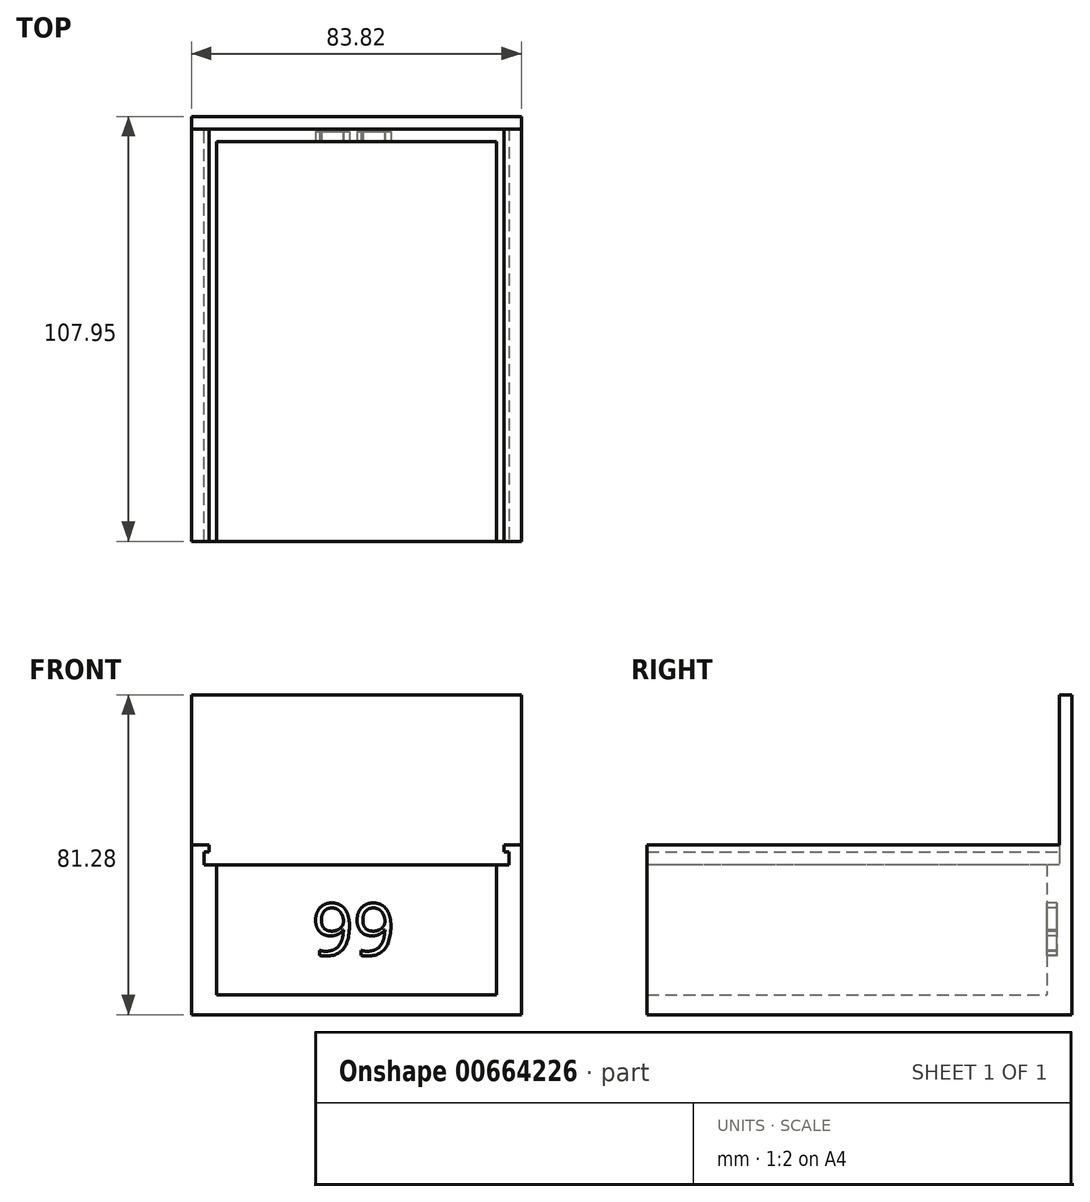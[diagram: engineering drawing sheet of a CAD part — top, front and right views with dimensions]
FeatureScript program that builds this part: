
annotation { "Feature Type Name" : "Feature", "Feature Type Description" : "" }
export const myFeature = defineFeature(function(context is Context, id is Id, definition is map)
    precondition{}
    {
        {
            var Q0;
            Q0=qCreatedBy(makeId("Top.planeOp"),FACE);
            var sketch = newSketch(context, id + "F0", { "sketchPlane" : qUnion([Q0])});
            skLineSegment(sketch, "E0.bottom", {"start": v(-35.56, 53.94) * mm, "end": v(35.56, 53.94) * mm});
            skLineSegment(sketch, "E0.top", {"start": v(-35.56, -42.58) * mm, "end": v(35.56, -42.58) * mm});
            skLineSegment(sketch, "E0.left", {"start": v(-35.56, 53.94) * mm, "end": v(-35.56, -42.58) * mm});
            skLineSegment(sketch, "E0.right", {"start": v(35.56, 53.94) * mm, "end": v(35.56, -42.58) * mm});
            skPoint(sketch, "E0.middle", {"position": v(0, 5.68) * mm});
            skLineSegment(sketch, "E1.bottom", {"start": v(-38.73, 57.11) * mm, "end": v(38.74, 57.11) * mm});
            skLineSegment(sketch, "E1.top", {"start": v(-38.74, -45.76) * mm, "end": v(38.74, -45.76) * mm});
            skLineSegment(sketch, "E1.left", {"start": v(-38.73, 57.11) * mm, "end": v(-38.74, -45.76) * mm});
            skLineSegment(sketch, "E1.right", {"start": v(38.74, 57.11) * mm, "end": v(38.74, -45.76) * mm});
            skLineSegment(sketch, "E2.bottom", {"start": v(-41.9, 60.29) * mm, "end": v(41.91, 60.29) * mm});
            skLineSegment(sketch, "E2.top", {"start": v(-41.91, -48.93) * mm, "end": v(41.91, -48.93) * mm});
            skLineSegment(sketch, "E2.left", {"start": v(-41.9, 60.29) * mm, "end": v(-41.91, -48.93) * mm});
            skLineSegment(sketch, "E2.right", {"start": v(41.91, 60.29) * mm, "end": v(41.91, -48.93) * mm});
            skLineSegment(sketch, "E3", {"start": v(-35.56, -42.58) * mm, "end": v(-41.91, -42.58) * mm});
            skLineSegment(sketch, "E4", {"start": v(35.56, -42.58) * mm, "end": v(41.91, -42.58) * mm});
            skSolve(sketch);
        }
        {
            var Q0;
            {var subQ2=sQuery(id+"F0.wireOp",EDGE,"E1.bottom");Q0=makeQuery(id+"F0.imprint","IMPRINT",FACE,{"disambiguationData":[TD([[makeQuery(id+"F0.imprint","IMPRINT",EDGE,{"derivedFrom":subQ2}),1.0]])]});}
            extrude(context, id + "F1", {"entities" : qUnion([Q0]), "depth" : 50.8 * mm, "offsetDistance" : 25.4 * mm});
        }
        {
            var Q0;
            Q0=makeQuery(id+"F0.imprint","IMPRINT",FACE,{"disambiguationData":[TD([[makeQuery(id+"F0.imprint","IMPRINT",EDGE,{"derivedFrom":sQuery(id+"F0.wireOp",EDGE,"E0.bottom")}),-1.0]])]});
            var Q1;
            Q1=makeQuery(id+"F0.imprint","IMPRINT",FACE,{"disambiguationData":[TD([[makeQuery(id+"F0.imprint","IMPRINT",EDGE,{"derivedFrom":sQuery(id+"F0.wireOp",EDGE,"E0.bottom")}),1.0]])]});
            extrude(context, id + "F2", {"entities" : qUnion([Q0, Q1]), "operationType" : NewBodyOperationType.ADD, "depth" : 12.7 * mm, "offsetDistance" : 25.4 * mm});
        }
        {
            var Q0;
            Q0=makeQuery(id+"F0.imprint","IMPRINT",FACE,{"disambiguationData":[TD([[makeQuery(id+"F0.imprint","IMPRINT",EDGE,{"derivedFrom":sQuery(id+"F0.wireOp",EDGE,"E0.bottom")}),1.0]])]});
            extrude(context, id + "F3", {"entities" : qUnion([Q0]), "operationType" : NewBodyOperationType.ADD, "depth" : 45.72 * mm, "offsetDistance" : 25.4 * mm});
        }
        {
            var Q0;
            Q0=makeQuery(id+"F1.opExtrude","SWEPT_FACE",FACE,{"disambiguationData":[OSD([sQuery(id+"F0.wireOp",EDGE,"E1.left")])]});
            var sketch = newSketch(context, id + "F4", { "sketchPlane" : qUnion([Q0])});
            skLineSegment(sketch, "E5.bottom", {"start": v(-42.58, 50.8) * mm, "end": v(57.11, 50.8) * mm});
            skLineSegment(sketch, "E5.top", {"start": v(-42.58, 49.02) * mm, "end": v(57.11, 49.02) * mm});
            skLineSegment(sketch, "E5.left", {"start": v(-42.58, 50.8) * mm, "end": v(-42.58, 49.02) * mm});
            skLineSegment(sketch, "E5.right", {"start": v(57.11, 50.8) * mm, "end": v(57.11, 49.02) * mm});
            skSolve(sketch);
        }
        {
            var Q0;
            Q0 = qSketchRegion(id + "F4", true);
            extrude(context, id + "F5", {"entities" : qUnion([Q0]), "operationType" : NewBodyOperationType.ADD, "depth" : 1.27 * mm, "offsetDistance" : 25.4 * mm});
        }
        {
            var Q0;
            Q0=makeQuery(id+"F1.opExtrude","SWEPT_FACE",FACE,{"disambiguationData":[OSD([sQuery(id+"F0.wireOp",EDGE,"E1.right")])]});
            var sketch = newSketch(context, id + "F6", { "sketchPlane" : qUnion([Q0])});
            skLineSegment(sketch, "E6.bottom", {"start": v(42.58, 50.8) * mm, "end": v(-57.11, 50.8) * mm});
            skLineSegment(sketch, "E6.top", {"start": v(42.58, 49.02) * mm, "end": v(-57.11, 49.02) * mm});
            skLineSegment(sketch, "E6.left", {"start": v(42.58, 50.8) * mm, "end": v(42.58, 49.02) * mm});
            skLineSegment(sketch, "E6.right", {"start": v(-57.11, 50.8) * mm, "end": v(-57.11, 49.02) * mm});
            skSolve(sketch);
        }
        {
            var Q0;
            Q0 = qSketchRegion(id + "F6", true);
            extrude(context, id + "F7", {"entities" : qUnion([Q0]), "operationType" : NewBodyOperationType.ADD, "depth" : 1.27 * mm, "offsetDistance" : 25.4 * mm});
        }
        {
            var Q0;
            Q0=makeQuery(id+"F3.opExtrude","SWEPT_FACE",FACE,{"disambiguationData":[OSD([sQuery(id+"F0.wireOp",EDGE,"E0.bottom")])]});
            var sketch = newSketch(context, id + "F8", { "sketchPlane" : qUnion([Q0])});
            skText(sketch, "E7", { "text": "99", "fontName": "OpenSans-Regular.ttf"});
            const initialGuessF8  = {"E7": [-0.01128, 0.02268, 1, 0, 0.01326]};
            skSetInitialGuess(sketch, initialGuessF8);
            skSolve(sketch);
        }
        {
            var Q0;
            Q0 = qSketchRegion(id + "F8", true);
            extrude(context, id + "F9", {"entities" : qUnion([Q0]), "operationType" : NewBodyOperationType.REMOVE, "oppositeDirection" : true, "depth" : 2.54 * mm, "offsetDistance" : 25.4 * mm});
        }
        {
            var Q0;
            {var subQ0=sQuery(id+"F0.wireOp",EDGE,"E4");var subQ1=sQuery(id+"F0.wireOp",EDGE,"E3");var subQ2=sQuery(id+"F0.wireOp",EDGE,"E1.right");var subQ3=sQuery(id+"F0.wireOp",EDGE,"E1.left");var subQ4=sQuery(id+"F0.wireOp",EDGE,"E1.bottom");Q0=makeQuery(id+"F2.boolean.opBoolean","MERGE",FACE,{"derivedFrom":[makeQuery(id+"F1.opExtrude","CAP_FACE",FACE,{"disambiguationData":[OSD([subQ4,subQ3,subQ2,sQuery(id+"F0.wireOp",EDGE,"E2.bottom"),sQuery(id+"F0.wireOp",EDGE,"E2.left"),sQuery(id+"F0.wireOp",EDGE,"E2.right"),subQ1,subQ0])],"isStart":true}),makeQuery(id+"F2.opExtrude","CAP_FACE",FACE,{"disambiguationData":[OSD([sQuery(id+"F0.wireOp",EDGE,"E0.top"),subQ4,subQ3,subQ2,subQ1,subQ0])],"isStart":true})]});}
            var sketch = newSketch(context, id + "F10", { "sketchPlane" : qUnion([Q0])});
            skLineSegment(sketch, "E8.bottom", {"start": v(-41.91, 42.58) * mm, "end": v(41.91, 42.58) * mm});
            skLineSegment(sketch, "E8.top", {"start": v(-41.91, -60.29) * mm, "end": v(41.91, -60.29) * mm});
            skLineSegment(sketch, "E8.left", {"start": v(-41.91, 42.58) * mm, "end": v(-41.91, -60.29) * mm});
            skLineSegment(sketch, "E8.right", {"start": v(41.91, 42.58) * mm, "end": v(41.91, -60.29) * mm});
            skSolve(sketch);
        }
        {
            var Q0;
            Q0 = qSketchRegion(id + "F10", true);
            extrude(context, id + "F11", {"entities" : qUnion([Q0]), "operationType" : NewBodyOperationType.REMOVE, "oppositeDirection" : true, "depth" : 7.62 * mm, "offsetDistance" : 25.4 * mm});
        }
        {
            var Q0;
            Q0=makeQuery(id+"F7.boolean.opBoolean","MERGE",FACE,{"derivedFrom":[makeQuery(id+"F5.boolean.opBoolean","MERGE",FACE,{"derivedFrom":[makeQuery(id+"F1.opExtrude","CAP_FACE",FACE,{"disambiguationData":[OSD([sQuery(id+"F0.wireOp",EDGE,"E1.bottom"),sQuery(id+"F0.wireOp",EDGE,"E1.left"),sQuery(id+"F0.wireOp",EDGE,"E1.right"),sQuery(id+"F0.wireOp",EDGE,"E2.bottom"),sQuery(id+"F0.wireOp",EDGE,"E2.left"),sQuery(id+"F0.wireOp",EDGE,"E2.right"),sQuery(id+"F0.wireOp",EDGE,"E3"),sQuery(id+"F0.wireOp",EDGE,"E4")])],"isStart":false}),makeQuery(id+"F5.opExtrude","SWEPT_FACE",FACE,{"disambiguationData":[OSD([sQuery(id+"F4.wireOp",EDGE,"E5.bottom")])]})]}),makeQuery(id+"F7.opExtrude","SWEPT_FACE",FACE,{"disambiguationData":[OSD([sQuery(id+"F6.wireOp",EDGE,"E6.bottom")])]})]});
            var sketch = newSketch(context, id + "F12", { "sketchPlane" : qUnion([Q0])});
            skLineSegment(sketch, "E9.bottom", {"start": v(-41.9, 60.29) * mm, "end": v(41.91, 60.29) * mm});
            skLineSegment(sketch, "E9.top", {"start": v(-41.9, 57.11) * mm, "end": v(41.91, 57.11) * mm});
            skLineSegment(sketch, "E9.left", {"start": v(-41.9, 60.29) * mm, "end": v(-41.9, 57.11) * mm});
            skLineSegment(sketch, "E9.right", {"start": v(41.91, 60.29) * mm, "end": v(41.91, 57.11) * mm});
            skSolve(sketch);
        }
        {
            var Q0;
            Q0 = qSketchRegion(id + "F12", true);
            extrude(context, id + "F13", {"entities" : qUnion([Q0]), "operationType" : NewBodyOperationType.ADD, "depth" : 38.1 * mm, "offsetDistance" : 25.4 * mm});
        }
        {
            var Q0;
            {var subQ0=sQuery(id+"F0.wireOp",EDGE,"E4");var subQ1=sQuery(id+"F0.wireOp",EDGE,"E3");Q0=makeQuery(id+"F7.boolean.opBoolean","MERGE",FACE,{"derivedFrom":[makeQuery(id+"F5.boolean.opBoolean","MERGE",FACE,{"derivedFrom":[makeQuery(id+"F3.boolean.opBoolean","MERGE",FACE,{"derivedFrom":[makeQuery(id+"F2.boolean.opBoolean","MERGE",FACE,{"derivedFrom":[makeQuery(id+"F1.opExtrude","SWEPT_FACE",FACE,{"disambiguationData":[OSD([subQ1])]}),makeQuery(id+"F1.opExtrude","SWEPT_FACE",FACE,{"disambiguationData":[OSD([subQ0])]}),makeQuery(id+"F2.opExtrude","SWEPT_FACE",FACE,{"disambiguationData":[OSD([sQuery(id+"F0.wireOp",EDGE,"E0.top"),subQ1,subQ0])]})]}),makeQuery(id+"F3.opExtrude","SWEPT_FACE",FACE,{"disambiguationData":[OSD([subQ1])]}),makeQuery(id+"F3.opExtrude","SWEPT_FACE",FACE,{"disambiguationData":[OSD([subQ0])]})]}),makeQuery(id+"F5.opExtrude","SWEPT_FACE",FACE,{"disambiguationData":[OSD([sQuery(id+"F4.wireOp",EDGE,"E5.left")])]})]}),makeQuery(id+"F7.opExtrude","SWEPT_FACE",FACE,{"disambiguationData":[OSD([sQuery(id+"F6.wireOp",EDGE,"E6.left")])]})]});}
            var sketch = newSketch(context, id + "F14", { "sketchPlane" : qUnion([Q0])});
            skLineSegment(sketch, "E10", {"start": v(-37.47, 50.8) * mm, "end": v(-41.91, 50.8) * mm});
            skLineSegment(sketch, "E11", {"start": v(-41.91, 50.8) * mm, "end": v(-41.91, 7.62) * mm});
            skLineSegment(sketch, "E12", {"start": v(-41.91, 7.62) * mm, "end": v(41.91, 7.62) * mm});
            skLineSegment(sketch, "E13", {"start": v(41.91, 7.62) * mm, "end": v(41.91, 50.8) * mm});
            skLineSegment(sketch, "E14", {"start": v(41.91, 50.8) * mm, "end": v(37.47, 50.8) * mm});
            skLineSegment(sketch, "E15", {"start": v(37.47, 50.8) * mm, "end": v(37.47, 49.02) * mm});
            skLineSegment(sketch, "E16", {"start": v(37.47, 49.02) * mm, "end": v(38.74, 49.02) * mm});
            skLineSegment(sketch, "E17", {"start": v(38.74, 49.02) * mm, "end": v(38.74, 45.72) * mm});
            skLineSegment(sketch, "E18", {"start": v(38.74, 45.72) * mm, "end": v(35.56, 45.72) * mm});
            skLineSegment(sketch, "E19", {"start": v(35.56, 45.72) * mm, "end": v(35.56, 12.7) * mm});
            skLineSegment(sketch, "E20", {"start": v(35.56, 12.7) * mm, "end": v(-35.56, 12.7) * mm});
            skLineSegment(sketch, "E21", {"start": v(-35.56, 12.7) * mm, "end": v(-35.56, 45.72) * mm});
            skLineSegment(sketch, "E22", {"start": v(-35.56, 45.72) * mm, "end": v(-38.74, 45.72) * mm});
            skLineSegment(sketch, "E23", {"start": v(-38.74, 45.72) * mm, "end": v(-38.74, 49.02) * mm});
            skLineSegment(sketch, "E24", {"start": v(-38.74, 49.02) * mm, "end": v(-37.47, 49.02) * mm});
            skLineSegment(sketch, "E25", {"start": v(-37.47, 49.02) * mm, "end": v(-37.47, 50.8) * mm});
            skSolve(sketch);
        }
        {
            var Q0;
            Q0 = qSketchRegion(id + "F14", true);
            extrude(context, id + "F15", {"entities" : qUnion([Q0]), "operationType" : NewBodyOperationType.ADD, "depth" : 5.08 * mm, "offsetDistance" : 25.4 * mm});
        }
    });
